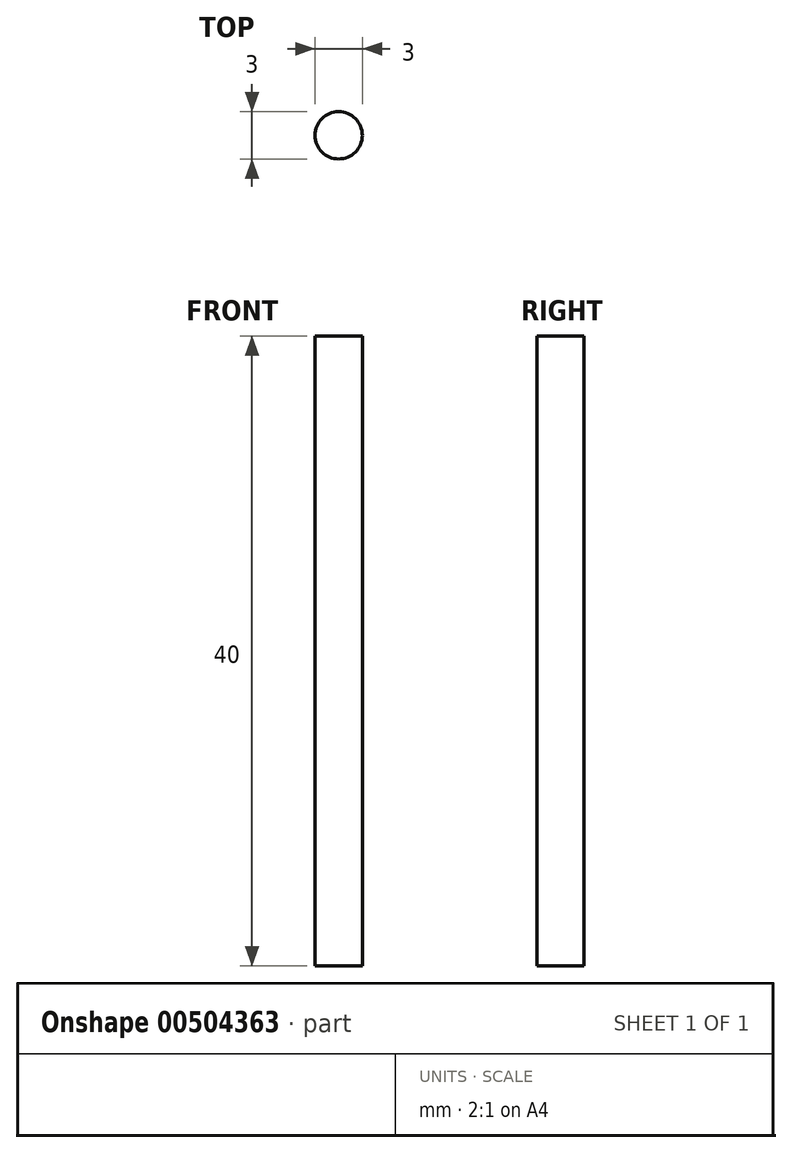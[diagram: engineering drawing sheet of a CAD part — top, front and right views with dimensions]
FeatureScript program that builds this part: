
annotation { "Feature Type Name" : "Feature", "Feature Type Description" : "" }
export const myFeature = defineFeature(function(context is Context, id is Id, definition is map)
    precondition{}
    {
        {
            var Q0;
            Q0=qCreatedBy(makeId("Front.planeOp"),FACE);
            var sketch = newSketch(context, id + "F0", { "sketchPlane" : qUnion([Q0])});
            skLineSegment(sketch, "E0.bottom", {"start": v(0, 30.3) * mm, "end": v(1.5, 30.3) * mm});
            skLineSegment(sketch, "E0.top", {"start": v(0, -9.7) * mm, "end": v(1.5, -9.7) * mm});
            skLineSegment(sketch, "E0.left", {"start": v(0, 30.3) * mm, "end": v(0, -9.7) * mm});
            skLineSegment(sketch, "E0.right", {"start": v(1.5, 30.3) * mm, "end": v(1.5, -9.7) * mm});
            skSolve(sketch);
        }
        {
            var Q0;
            Q0=makeQuery(id+"F0.imprint","IMPRINT",FACE,{"disambiguationData":[TD([[makeQuery(id+"F0.imprint","IMPRINT",EDGE,{"derivedFrom":sQuery(id+"F0.wireOp",EDGE,"E0.bottom")}),-1.0]])]});
            var Q1;
            Q1=sQuery(id+"F0.wireOp",EDGE,"E0.left");
            revolve(context, id + "F1", {"entities" : qUnion([Q0]), "axis" : qUnion([Q1]), "revolveType" : RevolveType.FULL});
        }
    });
